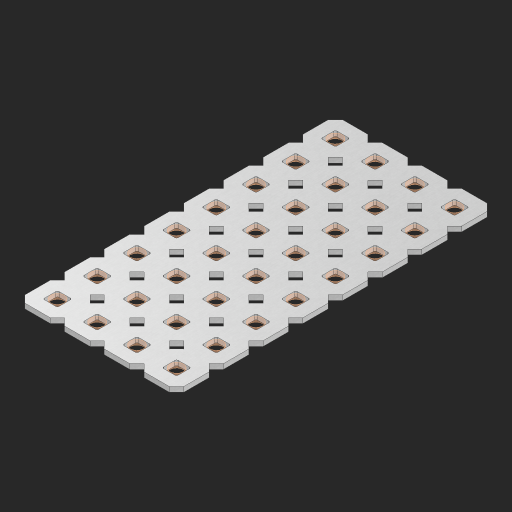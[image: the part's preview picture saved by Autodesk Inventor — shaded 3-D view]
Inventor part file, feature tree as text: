
AUTODESK INVENTOR PART (.ipt)
format: ipt  version: 2023 (Build 270158000, 158)  size: 671,232 bytes
history: native  units: in
note: dims shown in document units (in); Inventor stores cm internally (conversion verified against a paired STEP export)
features: other x33, extrude x31, sketch x2, pattern_linear x1
ambient origin geometry x8: Origin, YZ Plane, XZ Plane, XY Plane, X Axis, Y Axis, Z Axis, Center Point
bodies: Solid1 (feature_tree), Body (feature_tree)
feature tree (67):
  pattern_linear  "Rectangular Pattern1"  Spacing1=0.09in  [1 undecoded]
  sketch  "Sketch1"  dims[d1=0.5in]
  sketch  "Sketch2"  dims[d2=0.182in d3=0.09in d4=0.09in d5=0.09in d6=0.09in d7=0.09in d8=0.09in d9=0.09in d10=0.09in d11=0.02in d13=0.0in d14=0.172in d15=0.0625in d16=0.0in d19=0.5in d22=0.5in]
  other  "Srf1"
  other  "Srf126"
  other  "Srf127"
  other  "Srf128"
  other  "Srf129"
  other  "Srf130"
  other  "Srf131"
  other  "Srf250"
  other  "Srf268"
  other  "Srf269"
  other  "Srf270"
  other  "Srf271"
  other  "Srf272"
  other  "Srf273"
  other  "Srf274"
  other  "Srf275"
  other  "Srf293"
  other  "Srf294"
  other  "Srf295"
  other  "Srf296"
  other  "Srf297"
  other  "Srf298"
  other  "Srf299"
  other  "Srf300"
  other  "Srf318"
  other  "Srf319"
  other  "Srf320"
  other  "Srf321"
  other  "Srf322"
  other  "Srf323"
  other  "Srf324"
  other  "Srf325"
  other  "Circle"
  extrude  "ExtrusionSrf126"  Depth=0.09in
  extrude  "ExtrusionSrf127"  Depth=0.09in
  extrude  "ExtrusionSrf128"  Depth=0.09in
  extrude  "ExtrusionSrf129"  Depth=0.09in
  extrude  "ExtrusionSrf130"  Depth=0.09in
  extrude  "ExtrusionSrf131"  Depth=0.09in
  extrude  "ExtrusionSrf250"  Depth=0.09in
  extrude  "ExtrusionSrf268"  Depth=0.02in
  extrude  "ExtrusionSrf269"  TaperAngle=0.0deg  [1 undecoded]
  extrude  "ExtrusionSrf270"  Depth=0.5in
  extrude  "ExtrusionSrf271"  Depth=0.0625in TaperAngle=0.0deg
  extrude  "ExtrusionSrf272"  Depth=0.5in
  extrude  "ExtrusionSrf273"  Depth=0.5in
  extrude  "ExtrusionSrf274"  [1 undecoded]
  extrude  "ExtrusionSrf275"  [1 undecoded]
  extrude  "ExtrusionSrf293"  [1 undecoded]
  extrude  "ExtrusionSrf294"  [1 undecoded]
  extrude  "ExtrusionSrf295"  [1 undecoded]
  extrude  "ExtrusionSrf296"  [1 undecoded]
  extrude  "ExtrusionSrf297"  [1 undecoded]
  extrude  "ExtrusionSrf298"  [1 undecoded]
  extrude  "ExtrusionSrf299"  [1 undecoded]
  extrude  "ExtrusionSrf300"  [1 undecoded]
  extrude  "ExtrusionSrf318"  [1 undecoded]
  extrude  "ExtrusionSrf319"  [1 undecoded]
  extrude  "ExtrusionSrf320"  [1 undecoded]
  extrude  "ExtrusionSrf321"  [1 undecoded]
  extrude  "ExtrusionSrf322"  [1 undecoded]
  extrude  "ExtrusionSrf323"  [1 undecoded]
  extrude  "ExtrusionSrf324"  [1 undecoded]
  extrude  "ExtrusionSrf325"  [1 undecoded]
note: 20 required parameter values undecoded (feature->parameter linkage not recoverable at this tier; creation-order binding heuristic only, values carry confidence <= 0.55)
